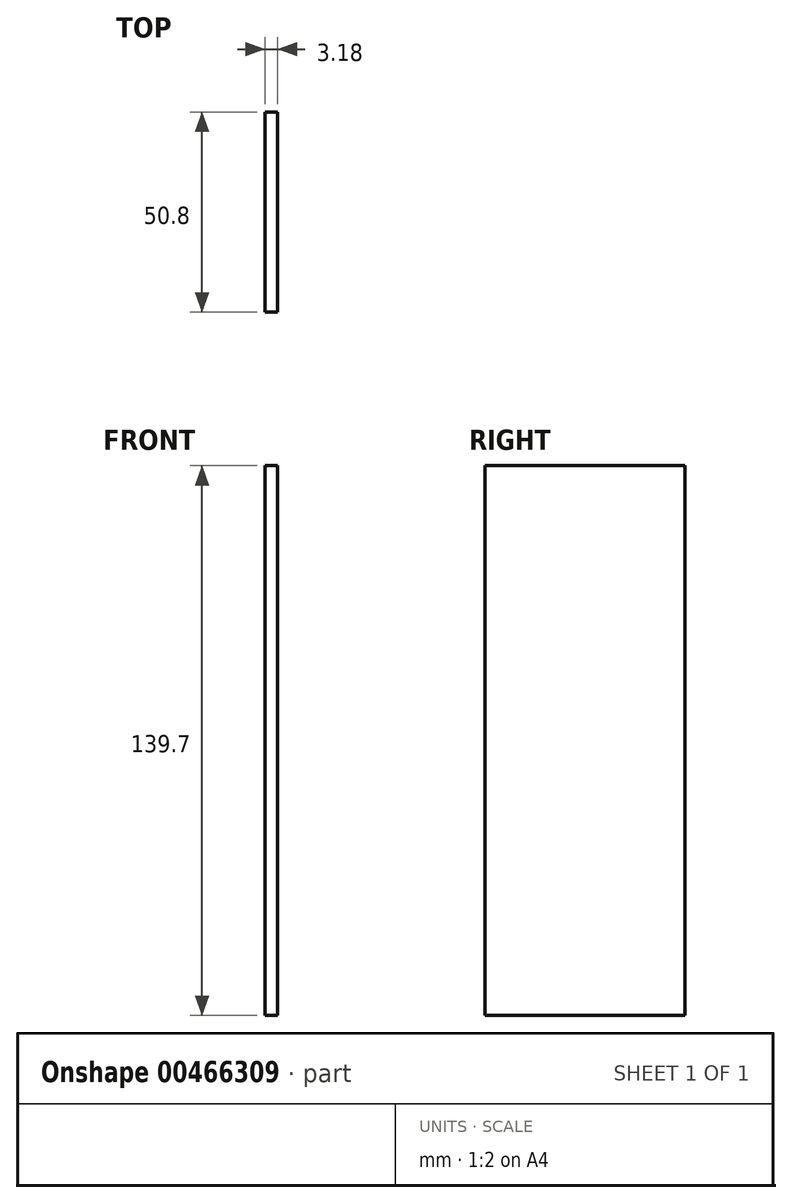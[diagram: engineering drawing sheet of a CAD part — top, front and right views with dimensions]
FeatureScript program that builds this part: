
annotation { "Feature Type Name" : "Feature", "Feature Type Description" : "" }
export const myFeature = defineFeature(function(context is Context, id is Id, definition is map)
    precondition{}
    {
        {
            var Q0;
            Q0=qCreatedBy(makeId("Front.planeOp"),FACE);
            var sketch = newSketch(context, id + "F0", { "sketchPlane" : qUnion([Q0])});
            skLineSegment(sketch, "E0", {"start": v(-45.8, 77.77) * mm, "end": v(-45.8, -61.93) * mm});
            skLineSegment(sketch, "E1", {"start": v(-45.8, -61.93) * mm, "end": v(-48.97, -61.93) * mm});
            skLineSegment(sketch, "E2", {"start": v(-48.97, 77.77) * mm, "end": v(-48.97, -61.93) * mm});
            skLineSegment(sketch, "E3", {"start": v(-45.8, 77.77) * mm, "end": v(-48.97, 77.77) * mm});
            skSolve(sketch);
        }
        {
            var Q0;
            Q0=makeQuery(id+"F0.imprint","IMPRINT",FACE,{"disambiguationData":[TD([[makeQuery(id+"F0.imprint","IMPRINT",EDGE,{"derivedFrom":sQuery(id+"F0.wireOp",EDGE,"E0")}),-1.0]])]});
            extrude(context, id + "F1", {"entities" : qUnion([Q0]), "depth" : 50.8 * mm});
        }
    });
